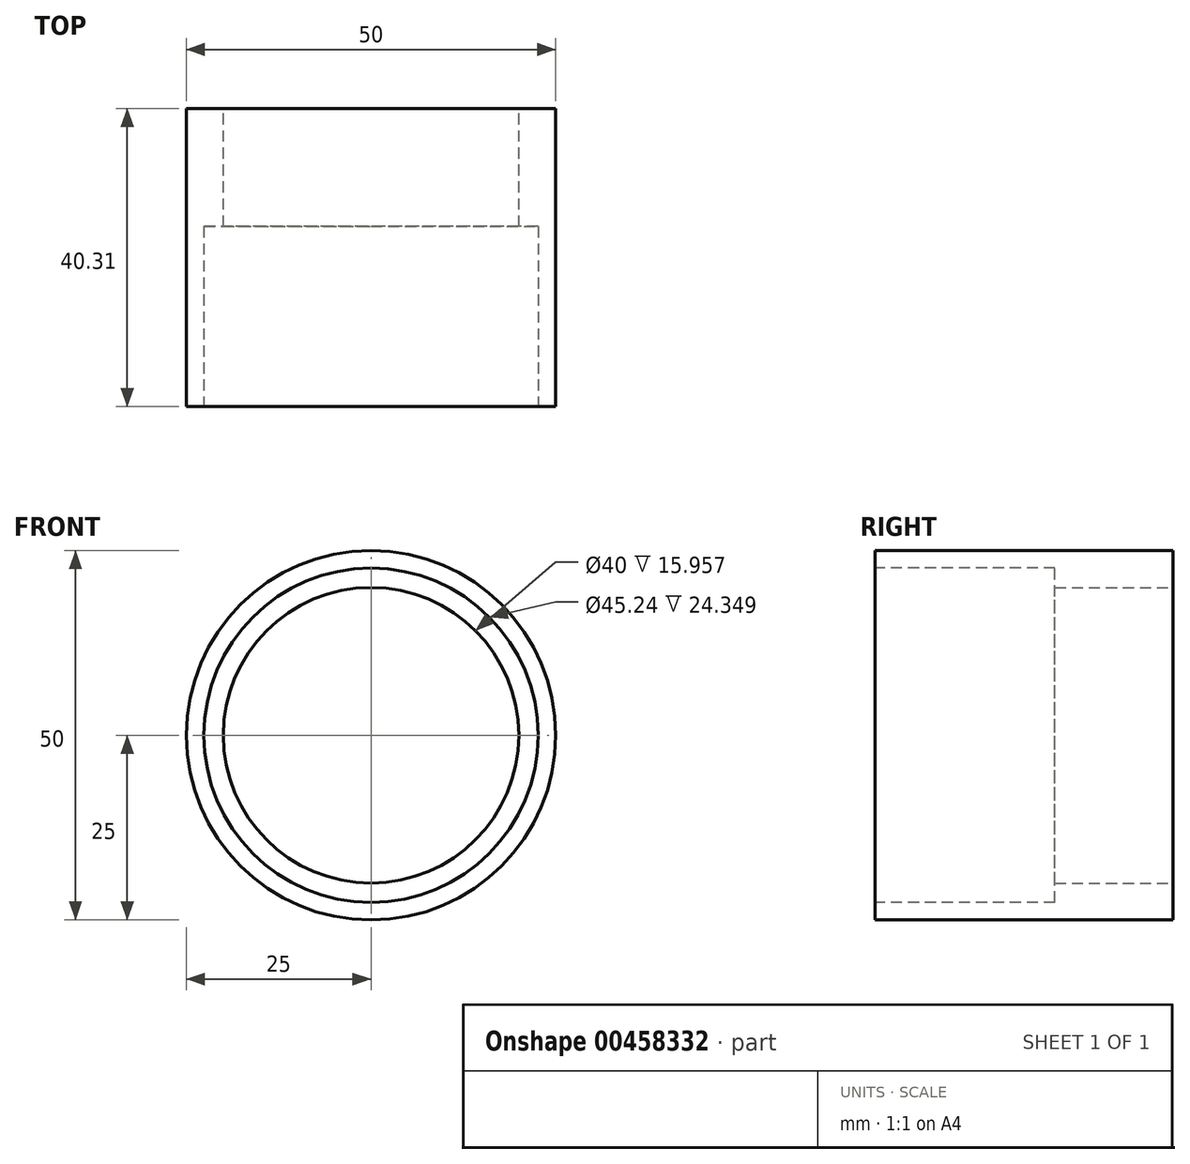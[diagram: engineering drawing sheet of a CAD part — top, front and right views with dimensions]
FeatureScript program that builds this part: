
annotation { "Feature Type Name" : "Feature", "Feature Type Description" : "" }
export const myFeature = defineFeature(function(context is Context, id is Id, definition is map)
    precondition{}
    {
        {
            var Q0;
            Q0=qCreatedBy(makeId("Front.planeOp"),FACE);
            var sketch = newSketch(context, id + "F0", { "sketchPlane" : qUnion([Q0])});
            skCircle(sketch, "E0", {"center": v(0, 0) * mm, "radius": 25 * mm});
            skCircle(sketch, "E1", {"center": v(0, 0) * mm, "radius": 20 * mm});
            skSolve(sketch);
        }
        {
            var Q0;
            Q0=makeQuery(id+"F0.imprint","IMPRINT",FACE,{"disambiguationData":[TD([[makeQuery(id+"F0.imprint","IMPRINT",EDGE,{"derivedFrom":sQuery(id+"F0.wireOp",EDGE,"E0")}),1.0]])]});
            extrude(context, id + "F1", {"entities" : qUnion([Q0]), "depth" : 40.3 * mm, "offsetDistance" : 25 * mm});
        }
        {
            var Q0;
            Q0=makeQuery(id+"F1.opExtrude","CAP_FACE",FACE,{"disambiguationData":[OSD([sQuery(id+"F0.wireOp",EDGE,"E0"),sQuery(id+"F0.wireOp",EDGE,"E1")])],"isStart":false});
            var sketch = newSketch(context, id + "F2", { "sketchPlane" : qUnion([Q0])});
            skCircle(sketch, "E2", {"center": v(0, 0) * mm, "radius": 22.62 * mm});
            skSolve(sketch);
        }
        {
            var Q0;
            Q0 = qSketchRegion(id + "F2", true);
            extrude(context, id + "F3", {"entities" : qUnion([Q0]), "operationType" : NewBodyOperationType.REMOVE, "oppositeDirection" : true, "depth" : 24.35 * mm, "offsetDistance" : 25 * mm});
        }
    });
